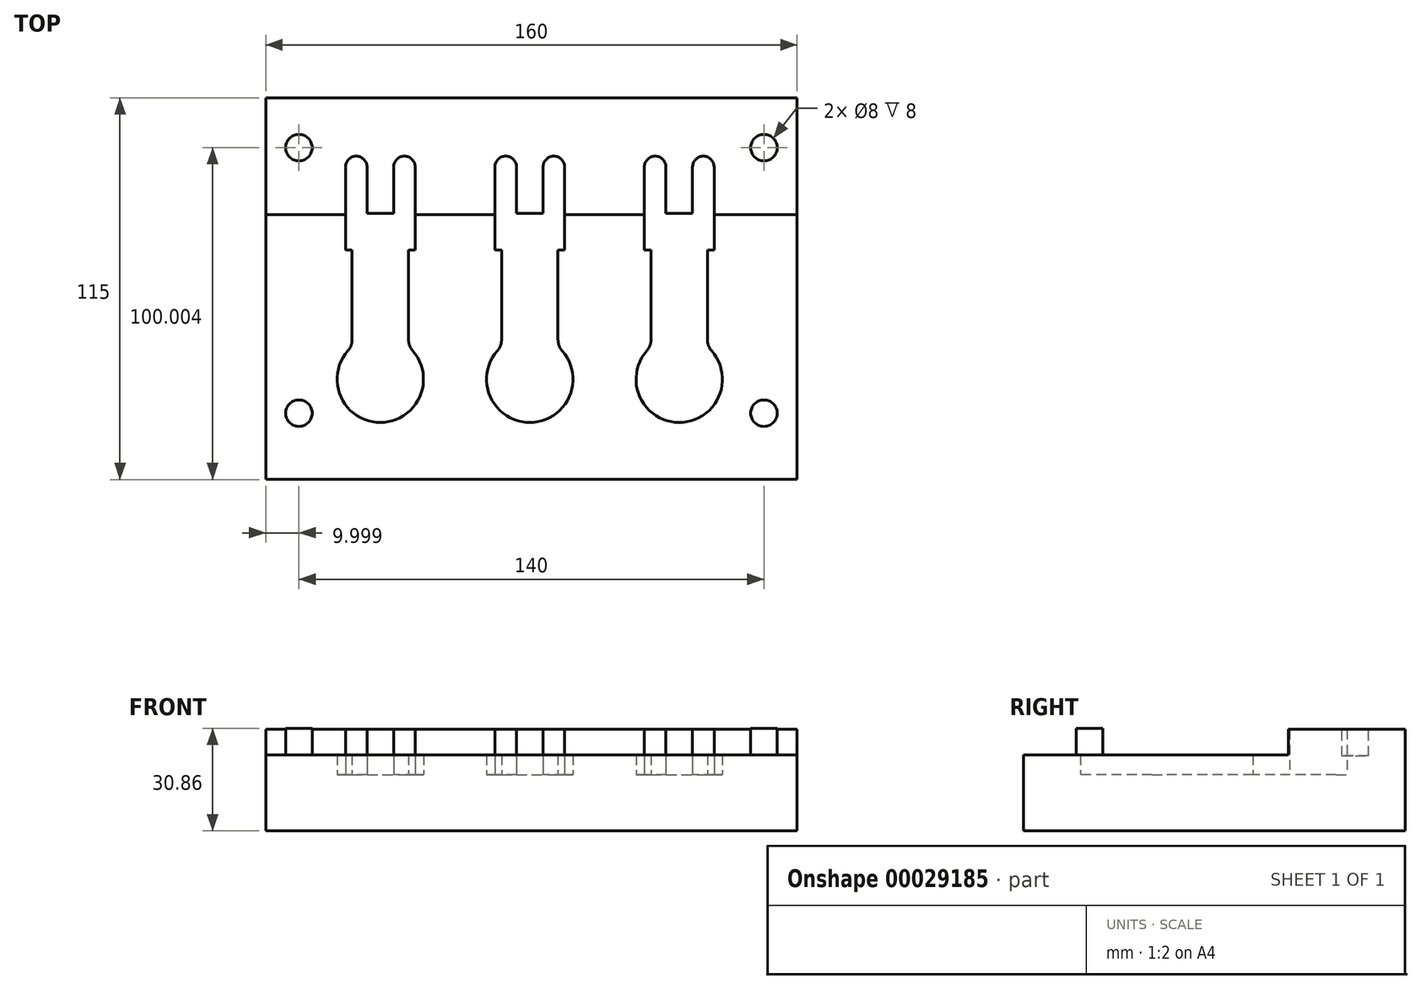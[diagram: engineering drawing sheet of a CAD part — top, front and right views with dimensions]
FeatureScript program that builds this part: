
annotation { "Feature Type Name" : "Feature", "Feature Type Description" : "" }
export const myFeature = defineFeature(function(context is Context, id is Id, definition is map)
    precondition{}
    {
        {
            var Q0;
            Q0=qCreatedBy(makeId("Top.planeOp"),FACE);
            var sketch = newSketch(context, id + "F0", { "sketchPlane" : qUnion([Q0])});
            skLineSegment(sketch, "E0.top", {"start": v(-85.13, 11.8) * mm, "end": v(-83.13, 11.8) * mm});
            skLineSegment(sketch, "E0.left", {"start": v(-85.13, 36.8) * mm, "end": v(-85.13, 11.8) * mm});
            skLineSegment(sketch, "E0.right", {"start": v(-64.13, 36.8) * mm, "end": v(-64.13, 11.8) * mm});
            skLineSegment(sketch, "E1.top", {"start": v(-78.63, 22.8) * mm, "end": v(-70.63, 22.8) * mm});
            skLineSegment(sketch, "E1.left", {"start": v(-78.63, 36.8) * mm, "end": v(-78.63, 22.8) * mm});
            skLineSegment(sketch, "E1.right", {"start": v(-70.63, 36.8) * mm, "end": v(-70.63, 22.8) * mm});
            skLineSegment(sketch, "E2.left", {"start": v(-83.13, 11.8) * mm, "end": v(-83.13, -15.3) * mm});
            skLineSegment(sketch, "E2.right", {"start": v(-66.13, 11.8) * mm, "end": v(-66.13, -15.3) * mm});
            skArc(sketch, "E3", {"start": v(-84.38, -18.6) * mm, "mid": v(-74.63, -40.2) * mm, "end": v(-64.88, -18.6) * mm});
            skLineSegment(sketch, "E4", {"start": v(-74.63, 22.8) * mm, "end": v(-74.63, -62.63) * mm, "construction": true});
            skPoint(sketch, "E5.visualSharp", {"position": v(-66.13, -17.37) * mm});
            skArc(sketch, "E5.filletArc", {"start": v(-66.13, -15.3) * mm, "mid": v(-65.8, -17.07) * mm, "end": v(-64.88, -18.6) * mm});
            skPoint(sketch, "E6.visualSharp", {"position": v(-83.13, -17.37) * mm});
            skArc(sketch, "E6.filletArc", {"start": v(-84.38, -18.6) * mm, "mid": v(-83.45, -17.07) * mm, "end": v(-83.13, -15.3) * mm});
            skPoint(sketch, "E7.visualSharp", {"position": v(-64.13, 11.8) * mm});
            skLineSegment(sketch, "E7.filletArc", {"start": v(-64.13, 11.8) * mm, "end": v(-64.13, 11.8) * mm});
            skPoint(sketch, "E8.visualSharp", {"position": v(-85.13, 11.8) * mm});
            skLineSegment(sketch, "E8.filletArc", {"start": v(-85.13, 11.8) * mm, "end": v(-85.13, 11.8) * mm});
            skLineSegment(sketch, "E9.trimOffspring", {"start": v(-66.13, 11.8) * mm, "end": v(-64.13, 11.8) * mm});
            skPoint(sketch, "E10.visualSharp", {"position": v(-83.13, 11.8) * mm});
            skLineSegment(sketch, "E10.filletArc", {"start": v(-83.13, 11.8) * mm, "end": v(-83.13, 11.8) * mm});
            skPoint(sketch, "E11.visualSharp", {"position": v(-66.13, 11.8) * mm});
            skLineSegment(sketch, "E11.filletArc", {"start": v(-66.13, 11.8) * mm, "end": v(-66.13, 11.8) * mm});
            skCircle(sketch, "E12", {"center": v(-74.63, -27.2) * mm, "radius": 6.75 * mm});
            skArc(sketch, "E13", {"start": v(-78.63, 36.8) * mm, "mid": v(-81.88, 40.05) * mm, "end": v(-85.13, 36.8) * mm});
            skArc(sketch, "E14", {"start": v(-64.13, 36.8) * mm, "mid": v(-67.38, 40.05) * mm, "end": v(-70.63, 36.8) * mm});
            skSolve(sketch);
        }
        {
            var Q0;
            Q0=makeQuery(id+"F0.imprint","IMPRINT",FACE,{"disambiguationData":[TD([[makeQuery(id+"F0.imprint","IMPRINT",EDGE,{"derivedFrom":sQuery(id+"F0.wireOp",EDGE,"E12")}),1.0]])]});
            var Q1;
            Q1=makeQuery(id+"F0.imprint","IMPRINT",FACE,{"disambiguationData":[TD([[makeQuery(id+"F0.imprint","IMPRINT",EDGE,{"derivedFrom":sQuery(id+"F0.wireOp",EDGE,"E0.top")}),1.0]])]});
            extrude(context, id + "F1", {"entities" : qUnion([Q0, Q1]), "depth" : 18 * mm});
        }
        {
            var Q0;
            Q0=qCreatedBy(makeId("Right.planeOp"),FACE);
            var sketch = newSketch(context, id + "F2", { "sketchPlane" : qUnion([Q0])});
            skLineSegment(sketch, "E15", {"start": v(-40.29, 25.83) * mm, "end": v(15.45, 25.83) * mm});
            skLineSegment(sketch, "E16", {"start": v(15.45, 25.83) * mm, "end": v(15.45, 18) * mm});
            skLineSegment(sketch, "E17", {"start": v(-10.3, 9) * mm, "end": v(-41.5, 9) * mm});
            skLineSegment(sketch, "E18", {"start": v(-41.5, 9) * mm, "end": v(-40.29, 25.83) * mm});
            skLineSegment(sketch, "E19", {"start": v(15.45, 18) * mm, "end": v(10.3, 18) * mm});
            skLineSegment(sketch, "E20", {"start": v(10.3, 18) * mm, "end": v(10.3, 16.2) * mm});
            skLineSegment(sketch, "E21", {"start": v(10.3, 16.2) * mm, "end": v(5.15, 16.2) * mm});
            skLineSegment(sketch, "E22", {"start": v(5.15, 16.2) * mm, "end": v(5.15, 14.4) * mm});
            skLineSegment(sketch, "E23", {"start": v(5.15, 14.4) * mm, "end": v(0, 14.4) * mm});
            skLineSegment(sketch, "E24", {"start": v(0, 14.4) * mm, "end": v(0, 12.6) * mm});
            skLineSegment(sketch, "E25", {"start": v(0, 12.6) * mm, "end": v(-5.15, 12.6) * mm});
            skLineSegment(sketch, "E26", {"start": v(-5.15, 12.6) * mm, "end": v(-5.15, 10.8) * mm});
            skLineSegment(sketch, "E27", {"start": v(-5.15, 10.8) * mm, "end": v(-10.3, 10.8) * mm});
            skLineSegment(sketch, "E28", {"start": v(-10.3, 10.8) * mm, "end": v(-10.3, 9) * mm});
            skSolve(sketch);
        }
        {
            var Q0;
            Q0=qSketchRegion(id+"F2",true);
            extrude(context, id + "F3", {"entities" : qUnion([Q0]), "operationType" : NewBodyOperationType.REMOVE, "oppositeDirection" : true, "depth" : 125 * mm});
        }
        {
            var Q0;
            Q0=makeQuery(id+"F3.boolean.opBoolean","COPY",FACE,{"derivedFrom":makeQuery(id+"F3.opExtrude","SWEPT_FACE",FACE,{"disambiguationData":[OSD([sQuery(id+"F2.wireOp",EDGE,"E17")])]})});
            var sketch = newSketch(context, id + "F4", { "sketchPlane" : qUnion([Q0])});
            skCircle(sketch, "E29", {"center": v(-74.63, -27.2) * mm, "radius": 8.3 * mm});
            skSolve(sketch);
        }
        {
            var Q0;
            Q0=qSketchRegion(id+"F4",true);
            extrude(context, id + "F5", {"entities" : qUnion([Q0]), "operationType" : NewBodyOperationType.REMOVE, "oppositeDirection" : true, "depth" : 3 * mm});
        }
        {
            var Q0;
            Q0=makeQuery(id+"F1.opExtrude","SWEPT_FACE",FACE,{"disambiguationData":[OSD([sQuery(id+"F0.wireOp",EDGE,"E0.right")])]});
            var sketch = newSketch(context, id + "F6", { "sketchPlane" : qUnion([Q0])});
            skCircle(sketch, "E30", {"center": v(30.8, 6) * mm, "radius": 2.5 * mm});
            skSolve(sketch);
        }
        {
            var Q0;
            Q0=makeQuery(id+"F1.opExtrude","SWEPT_FACE",FACE,{"disambiguationData":[OSD([sQuery(id+"F0.wireOp",EDGE,"E0.right")])]});
            var sketch = newSketch(context, id + "F7", { "sketchPlane" : qUnion([Q0])});
            skLineSegment(sketch, "E31", {"start": v(22.77, 0) * mm, "end": v(12.77, 0) * mm, "construction": true});
            skLineSegment(sketch, "E32", {"start": v(22.77, 0) * mm, "end": v(22.77, 17.98) * mm, "construction": true});
            skLineSegment(sketch, "E33", {"start": v(22.77, 17.98) * mm, "end": v(15.77, 17.98) * mm, "construction": true});
            skLineSegment(sketch, "E34", {"start": v(9.68, 20.3) * mm, "end": v(9.22, -2.99) * mm});
            skLineSegment(sketch, "E35", {"start": v(9.22, -2.99) * mm, "end": v(12.1, -2.99) * mm});
            skLineSegment(sketch, "E36", {"start": v(12.1, -2.99) * mm, "end": v(12.77, 0) * mm});
            skLineSegment(sketch, "E37", {"start": v(9.68, 20.3) * mm, "end": v(16.08, 19.87) * mm});
            skLineSegment(sketch, "E38", {"start": v(12.77, 0) * mm, "end": v(16.08, 19.87) * mm});
            skSolve(sketch);
        }
        {
            var Q0;
            Q0=makeQuery(id+"F1.opExtrude","SWEPT_FACE",FACE,{"disambiguationData":[OSD([sQuery(id+"F0.wireOp",EDGE,"E0.left")])]});
            var sketch = newSketch(context, id + "F8", { "sketchPlane" : qUnion([Q0])});
            skLineSegment(sketch, "E39", {"start": v(-12.8, 0) * mm, "end": v(-15.71, 18) * mm});
            skLineSegment(sketch, "E40", {"start": v(-15.71, 18) * mm, "end": v(-12.42, 21.29) * mm});
            skLineSegment(sketch, "E41", {"start": v(-12.42, 21.29) * mm, "end": v(-9.36, 20.22) * mm});
            skLineSegment(sketch, "E42", {"start": v(-9.36, 20.22) * mm, "end": v(-8.88, -2.86) * mm});
            skLineSegment(sketch, "E43", {"start": v(-8.88, -2.86) * mm, "end": v(-12.32, -2.93) * mm});
            skLineSegment(sketch, "E44", {"start": v(-12.32, -2.93) * mm, "end": v(-12.8, 0) * mm});
            skSolve(sketch);
        }
        {
            var Q0;
            Q0=makeQuery(id+"F1.opExtrude","SWEPT_FACE",FACE,{"disambiguationData":[OSD([sQuery(id+"F0.wireOp",EDGE,"E0.right")])]});
            var sketch = newSketch(context, id + "F9", { "sketchPlane" : qUnion([Q0])});
            skLineSegment(sketch, "E45", {"start": v(-57.39, 6) * mm, "end": v(-57.39, 32.33) * mm});
            skLineSegment(sketch, "E46", {"start": v(-57.39, 32.33) * mm, "end": v(57.61, 32.33) * mm});
            skLineSegment(sketch, "E47", {"start": v(57.61, 32.33) * mm, "end": v(57.61, 13.72) * mm});
            skLineSegment(sketch, "E48", {"start": v(57.61, 13.72) * mm, "end": v(57.61, -16.86) * mm});
            skLineSegment(sketch, "E49", {"start": v(57.61, -16.86) * mm, "end": v(-57.39, -16.86) * mm});
            skLineSegment(sketch, "E50", {"start": v(-57.39, -16.86) * mm, "end": v(-57.39, 6) * mm});
            skLineSegment(sketch, "E51", {"start": v(-57.39, 6) * mm, "end": v(22.49, 6) * mm});
            skLineSegment(sketch, "E52", {"start": v(22.49, 13.72) * mm, "end": v(22.49, 6) * mm});
            skLineSegment(sketch, "E53", {"start": v(22.49, 13.72) * mm, "end": v(57.61, 13.72) * mm});
            skSolve(sketch);
        }
        {
            var Q0;
            Q0=makeQuery(id+"F1.opExtrude","CAP_FACE",FACE,{"disambiguationData":[OSD([sQuery(id+"F0.wireOp",EDGE,"E0.top"),sQuery(id+"F0.wireOp",EDGE,"E0.left"),sQuery(id+"F0.wireOp",EDGE,"E0.right"),sQuery(id+"F0.wireOp",EDGE,"E1.top"),sQuery(id+"F0.wireOp",EDGE,"E1.left"),sQuery(id+"F0.wireOp",EDGE,"E1.right"),sQuery(id+"F0.wireOp",EDGE,"E2.left"),sQuery(id+"F0.wireOp",EDGE,"E2.right"),sQuery(id+"F0.wireOp",EDGE,"E3"),sQuery(id+"F0.wireOp",EDGE,"E5.filletArc"),sQuery(id+"F0.wireOp",EDGE,"E6.filletArc"),sQuery(id+"F0.wireOp",EDGE,"E9.trimOffspring"),sQuery(id+"F0.wireOp",EDGE,"E13"),sQuery(id+"F0.wireOp",EDGE,"E14")])],"isStart":false});
            var sketch = newSketch(context, id + "F10", { "sketchPlane" : qUnion([Q0])});
            skCircle(sketch, "E54", {"center": v(-74.58, 16.83) * mm, "radius": 5 * mm});
            skSolve(sketch);
        }
        {
            var Q0;
            Q0 = qSketchRegion(id + "F10", true);
            extrude(context, id + "F11", {"entities" : qUnion([Q0]), "operationType" : NewBodyOperationType.ADD, "depth" : 25 * mm, "hasDraft" : true, "draftAngle" : 10 * degree});
        }
        {
            var Q0;
            {var subQ8=sQuery(id+"F9.wireOp",EDGE,"E48");Q0=makeQuery(id+"F9.imprint","IMPRINT",FACE,{"disambiguationData":[TD([[makeQuery(id+"F9.imprint","IMPRINT",EDGE,{"derivedFrom":subQ8}),-1.0]])]});}
            var Q1;
            {var subQ8=sQuery(id+"F9.wireOp",EDGE,"E52");Q1=makeQuery(id+"F9.imprint","IMPRINT",FACE,{"disambiguationData":[TD([[makeQuery(id+"F9.imprint","IMPRINT",EDGE,{"derivedFrom":subQ8}),1.0]])]});}
            extrude(context, id + "F12", {"entities" : qUnion([Q0, Q1]), "depth" : 70 * mm, "hasSecondDirection" : true, "secondDirectionOppositeDirection" : true, "secondDirectionDepth" : 90 * mm});
        }
        {
            var Q0;
            Q0=makeQuery(id+"F12.opExtrude","SWEPT_FACE",FACE,{"disambiguationData":[OSD([sQuery(id+"F9.wireOp",EDGE,"E51")])]});
            var sketch = newSketch(context, id + "F13", { "sketchPlane" : qUnion([Q0])});
            skCircle(sketch, "E55", {"center": v(-144.13, -37.39) * mm, "radius": 4 * mm});
            skCircle(sketch, "E56", {"center": v(-4.13, -37.39) * mm, "radius": 4 * mm});
            skLineSegment(sketch, "E57", {"start": v(-144.13, -37.39) * mm, "end": v(-4.13, -37.39) * mm, "construction": true});
            skSolve(sketch);
        }
        {
            var Q0;
            Q0=makeQuery(id+"F12.opExtrude","SWEPT_FACE",FACE,{"disambiguationData":[OSD([sQuery(id+"F9.wireOp",EDGE,"E53")])]});
            var sketch = newSketch(context, id + "F14", { "sketchPlane" : qUnion([Q0])});
            skCircle(sketch, "E58", {"center": v(-144.13, 42.61) * mm, "radius": 4 * mm});
            skCircle(sketch, "E59", {"center": v(-4.13, 42.61) * mm, "radius": 4 * mm});
            skLineSegment(sketch, "E60", {"start": v(-144.13, 42.61) * mm, "end": v(-4.13, 42.61) * mm, "construction": true});
            skSolve(sketch);
        }
        {
            var Q0;
            Q0=makeQuery(id+"F14.imprint","IMPRINT",FACE,{"disambiguationData":[TD([[makeQuery(id+"F14.imprint","IMPRINT",EDGE,{"derivedFrom":sQuery(id+"F14.wireOp",EDGE,"E58")}),1.0]])]});
            var Q1;
            Q1=makeQuery(id+"F14.imprint","IMPRINT",FACE,{"disambiguationData":[TD([[makeQuery(id+"F14.imprint","IMPRINT",EDGE,{"derivedFrom":sQuery(id+"F14.wireOp",EDGE,"E59")}),1.0]])]});
            extrude(context, id + "F15", {"entities" : qUnion([Q0, Q1]), "operationType" : NewBodyOperationType.REMOVE, "oppositeDirection" : true, "depth" : 8 * mm});
        }
        {
            var Q0;
            Q0=makeQuery(id+"F13.imprint","IMPRINT",FACE,{"disambiguationData":[TD([[makeQuery(id+"F13.imprint","IMPRINT",EDGE,{"derivedFrom":sQuery(id+"F13.wireOp",EDGE,"E55")}),1.0]])]});
            var Q1;
            Q1=makeQuery(id+"F13.imprint","IMPRINT",FACE,{"disambiguationData":[TD([[makeQuery(id+"F13.imprint","IMPRINT",EDGE,{"derivedFrom":sQuery(id+"F13.wireOp",EDGE,"E56")}),1.0]])]});
            extrude(context, id + "F16", {"entities" : qUnion([Q0, Q1]), "operationType" : NewBodyOperationType.ADD, "depth" : 8 * mm});
        }
        {
            var Q0;
            Q0=makeQuery(id+"F1.opExtrude","SWEPT_BODY",BODY,{"disambiguationData":[OSD([sQuery(id+"F0.wireOp",EDGE,"E0.top"),sQuery(id+"F0.wireOp",EDGE,"E0.left"),sQuery(id+"F0.wireOp",EDGE,"E0.right"),sQuery(id+"F0.wireOp",EDGE,"E1.top"),sQuery(id+"F0.wireOp",EDGE,"E1.left"),sQuery(id+"F0.wireOp",EDGE,"E1.right"),sQuery(id+"F0.wireOp",EDGE,"E2.left"),sQuery(id+"F0.wireOp",EDGE,"E2.right"),sQuery(id+"F0.wireOp",EDGE,"E3"),sQuery(id+"F0.wireOp",EDGE,"E5.filletArc"),sQuery(id+"F0.wireOp",EDGE,"E6.filletArc"),sQuery(id+"F0.wireOp",EDGE,"E9.trimOffspring"),sQuery(id+"F0.wireOp",EDGE,"E13"),sQuery(id+"F0.wireOp",EDGE,"E14")])]});
            transform(context, id + "F17", {"entities" : qUnion([Q0]), "transformType" : TransformType.TRANSLATION_3D, "dx" : 45 * mm, "dy" : 0 * mm, "dz" : 0 * mm, "makeCopy" : true});
        }
        {
            var Q0;
            Q0=makeQuery(id+"F1.opExtrude","SWEPT_BODY",BODY,{"disambiguationData":[OSD([sQuery(id+"F0.wireOp",EDGE,"E0.top"),sQuery(id+"F0.wireOp",EDGE,"E0.left"),sQuery(id+"F0.wireOp",EDGE,"E0.right"),sQuery(id+"F0.wireOp",EDGE,"E1.top"),sQuery(id+"F0.wireOp",EDGE,"E1.left"),sQuery(id+"F0.wireOp",EDGE,"E1.right"),sQuery(id+"F0.wireOp",EDGE,"E2.left"),sQuery(id+"F0.wireOp",EDGE,"E2.right"),sQuery(id+"F0.wireOp",EDGE,"E3"),sQuery(id+"F0.wireOp",EDGE,"E5.filletArc"),sQuery(id+"F0.wireOp",EDGE,"E6.filletArc"),sQuery(id+"F0.wireOp",EDGE,"E9.trimOffspring"),sQuery(id+"F0.wireOp",EDGE,"E13"),sQuery(id+"F0.wireOp",EDGE,"E14")])]});
            transform(context, id + "F18", {"entities" : qUnion([Q0]), "transformType" : TransformType.TRANSLATION_3D, "dx" : -45 * mm, "dy" : 0 * mm, "dz" : 0 * mm, "makeCopy" : true});
        }
        {
            var Q0;
            Q0=makeQuery(id+"F1.opExtrude","SWEPT_BODY",BODY,{"disambiguationData":[OSD([sQuery(id+"F0.wireOp",EDGE,"E0.bottom"),sQuery(id+"F0.wireOp",EDGE,"E0.top"),sQuery(id+"F0.wireOp",EDGE,"E0.left"),sQuery(id+"F0.wireOp",EDGE,"E0.right"),sQuery(id+"F0.wireOp",EDGE,"E1.top"),sQuery(id+"F0.wireOp",EDGE,"E1.left"),sQuery(id+"F0.wireOp",EDGE,"E1.right"),sQuery(id+"F0.wireOp",EDGE,"3b6ef628-da63-4f4e-a1c5-ea05c0a2540d.trimOffspring"),sQuery(id+"F0.wireOp",EDGE,"E2.left"),sQuery(id+"F0.wireOp",EDGE,"E2.right"),sQuery(id+"F0.wireOp",EDGE,"E3"),sQuery(id+"F0.wireOp",EDGE,"E5.filletArc"),sQuery(id+"F0.wireOp",EDGE,"E6.filletArc"),sQuery(id+"F0.wireOp",EDGE,"E9.trimOffspring")])]});
            var Q1;
            Q1=makeQuery(id+"F18.opPattern","COPY",BODY,{"derivedFrom":makeQuery(id+"F1.opExtrude","SWEPT_BODY",BODY,{"disambiguationData":[OSD([sQuery(id+"F0.wireOp",EDGE,"E0.top"),sQuery(id+"F0.wireOp",EDGE,"E0.left"),sQuery(id+"F0.wireOp",EDGE,"E0.right"),sQuery(id+"F0.wireOp",EDGE,"E1.top"),sQuery(id+"F0.wireOp",EDGE,"E1.left"),sQuery(id+"F0.wireOp",EDGE,"E1.right"),sQuery(id+"F0.wireOp",EDGE,"E2.left"),sQuery(id+"F0.wireOp",EDGE,"E2.right"),sQuery(id+"F0.wireOp",EDGE,"E3"),sQuery(id+"F0.wireOp",EDGE,"E5.filletArc"),sQuery(id+"F0.wireOp",EDGE,"E6.filletArc"),sQuery(id+"F0.wireOp",EDGE,"E9.trimOffspring"),sQuery(id+"F0.wireOp",EDGE,"E13"),sQuery(id+"F0.wireOp",EDGE,"E14")])]}),"instanceName":"1"});
            var Q2;
            Q2=makeQuery(id+"F17.opPattern","COPY",BODY,{"derivedFrom":makeQuery(id+"F1.opExtrude","SWEPT_BODY",BODY,{"disambiguationData":[OSD([sQuery(id+"F0.wireOp",EDGE,"E0.top"),sQuery(id+"F0.wireOp",EDGE,"E0.left"),sQuery(id+"F0.wireOp",EDGE,"E0.right"),sQuery(id+"F0.wireOp",EDGE,"E1.top"),sQuery(id+"F0.wireOp",EDGE,"E1.left"),sQuery(id+"F0.wireOp",EDGE,"E1.right"),sQuery(id+"F0.wireOp",EDGE,"E2.left"),sQuery(id+"F0.wireOp",EDGE,"E2.right"),sQuery(id+"F0.wireOp",EDGE,"E3"),sQuery(id+"F0.wireOp",EDGE,"E5.filletArc"),sQuery(id+"F0.wireOp",EDGE,"E6.filletArc"),sQuery(id+"F0.wireOp",EDGE,"E9.trimOffspring"),sQuery(id+"F0.wireOp",EDGE,"E13"),sQuery(id+"F0.wireOp",EDGE,"E14")])]}),"instanceName":"1"});
            var Q3;
            Q3=makeQuery(id+"F12.opExtrude","SWEPT_BODY",BODY,{"disambiguationData":[OSD([sQuery(id+"F9.wireOp",EDGE,"a7e27d74-994a-4891-aaa3-0980bfbdc30e"),sQuery(id+"F9.wireOp",EDGE,"fb911d7a-c046-4048-9a62-8b9bea53e43f"),sQuery(id+"F9.wireOp",EDGE,"E45"),sQuery(id+"F9.wireOp",EDGE,"E46"),sQuery(id+"F9.wireOp",EDGE,"E47"),sQuery(id+"F9.wireOp",EDGE,"ea3ffea4-3806-48fb-9a5a-532117da88c0")])]});
            var Q4;
            Q4=makeQuery(id+"F12.opExtrude","SWEPT_BODY",BODY,{"disambiguationData":[OSD([sQuery(id+"F9.wireOp",EDGE,"E48"),sQuery(id+"F9.wireOp",EDGE,"E49"),sQuery(id+"F9.wireOp",EDGE,"E50"),sQuery(id+"F9.wireOp",EDGE,"E51"),sQuery(id+"F9.wireOp",EDGE,"E52"),sQuery(id+"F9.wireOp",EDGE,"E53")])]});
            booleanBodies(context, id + "F19", {"operationType" : BooleanOperationType.SUBTRACTION, "tools" : qUnion([Q0, Q1, Q2]), "targets" : qUnion([Q3, Q4])});
        }
    });
